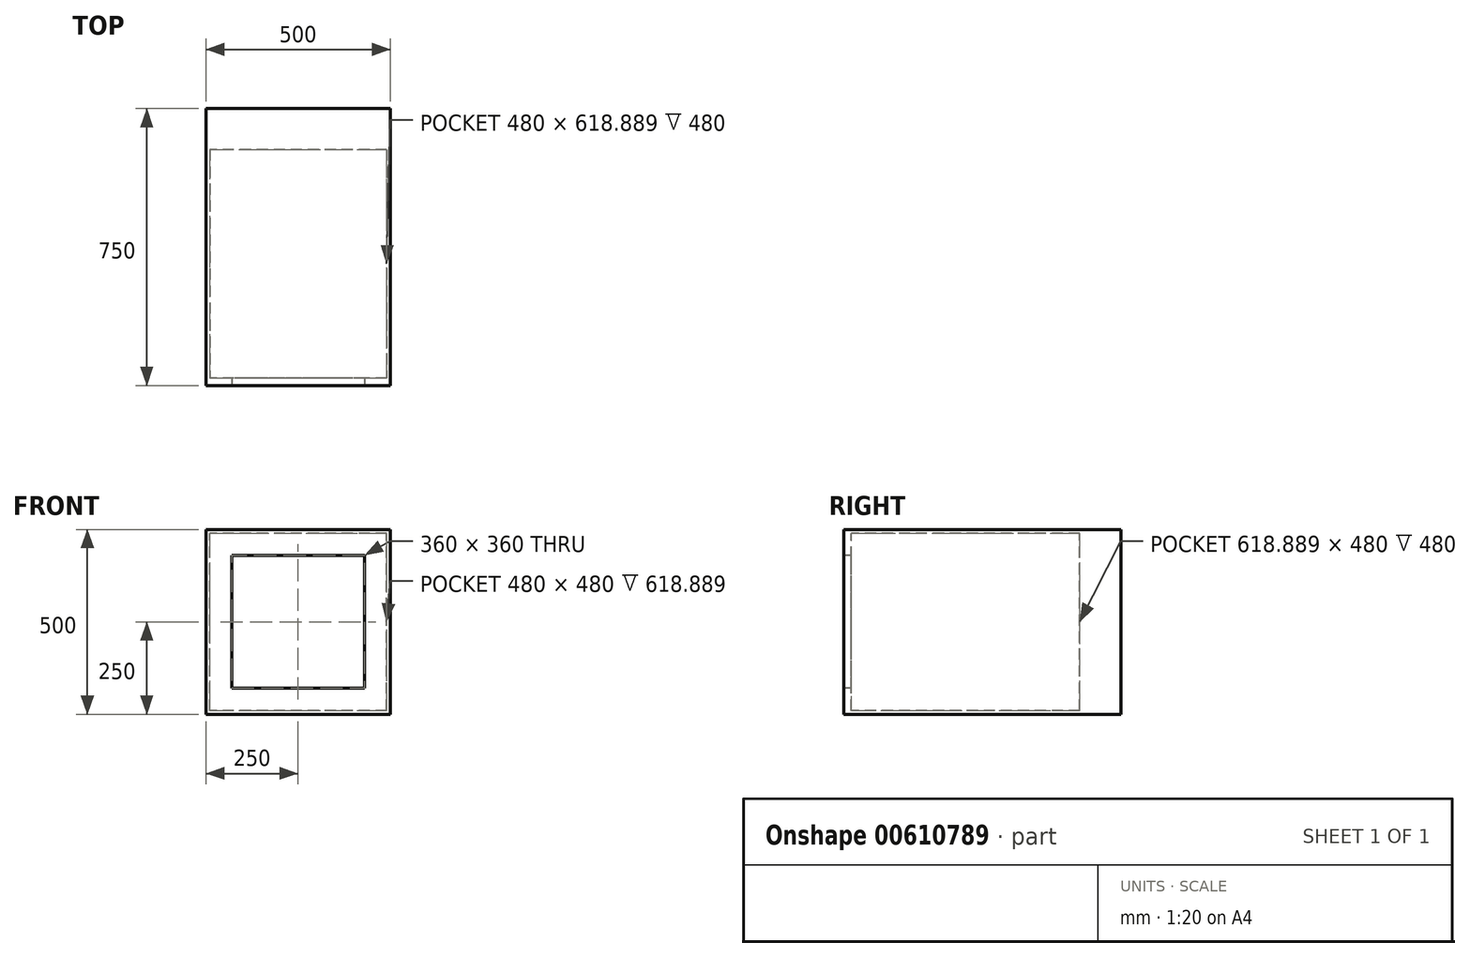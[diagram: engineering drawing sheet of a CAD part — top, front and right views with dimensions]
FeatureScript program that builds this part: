
annotation { "Feature Type Name" : "Feature", "Feature Type Description" : "" }
export const myFeature = defineFeature(function(context is Context, id is Id, definition is map)
    precondition{}
    {
        {
            var Q0;
            Q0=qCreatedBy(makeId("Front.planeOp"),FACE);
            var sketch = newSketch(context, id + "F0", { "sketchPlane" : qUnion([Q0])});
            skLineSegment(sketch, "E0.bottom", {"start": v(0, 0) * mm, "end": v(500, 0) * mm});
            skLineSegment(sketch, "E0.top", {"start": v(0, 500) * mm, "end": v(500, 500) * mm});
            skLineSegment(sketch, "E0.left", {"start": v(0, 0) * mm, "end": v(0, 500) * mm});
            skLineSegment(sketch, "E0.right", {"start": v(500, 0) * mm, "end": v(500, 500) * mm});
            skSolve(sketch);
        }
        {
            var Q0;
            Q0 = qSketchRegion(id + "F0", true);
            extrude(context, id + "F1", {"entities" : qUnion([Q0]), "depth" : 750 * mm, "offsetDistance" : 25 * mm});
        }
        {
            var Q0;
            Q0=makeQuery(id+"F1.opExtrude","CAP_FACE",FACE,{"disambiguationData":[OSD([sQuery(id+"F0.wireOp",EDGE,"E0.bottom"),sQuery(id+"F0.wireOp",EDGE,"E0.top"),sQuery(id+"F0.wireOp",EDGE,"E0.left"),sQuery(id+"F0.wireOp",EDGE,"E0.right")])],"isStart":false});
            var sketch = newSketch(context, id + "F2", { "sketchPlane" : qUnion([Q0])});
            skLineSegment(sketch, "E1", {"start": v(0, 0) * mm, "end": v(500, 500) * mm});
            skLineSegment(sketch, "E2.bottom", {"start": v(430, 70) * mm, "end": v(70, 70) * mm});
            skLineSegment(sketch, "E2.top", {"start": v(430, 430) * mm, "end": v(70, 430) * mm});
            skLineSegment(sketch, "E2.left", {"start": v(430, 70) * mm, "end": v(430, 430) * mm});
            skLineSegment(sketch, "E2.right", {"start": v(70, 70) * mm, "end": v(70, 430) * mm});
            skPoint(sketch, "E2.middle", {"position": v(250, 250) * mm});
            skSolve(sketch);
        }
        {
            var Q0;
            Q0 = qSketchRegion(id + "F2", true);
            extrude(context, id + "F3", {"entities" : qUnion([Q0]), "operationType" : NewBodyOperationType.REMOVE, "oppositeDirection" : true, "depth" : 20 * mm, "offsetDistance" : 25 * mm});
        }
        {
            var Q0;
            Q0=makeQuery(id+"F3.boolean.opBoolean","COPY",FACE,{"derivedFrom":makeQuery(id+"F3.opExtrude","CAP_FACE",FACE,{"disambiguationData":[OSD([sQuery(id+"F2.wireOp",EDGE,"E2.bottom"),sQuery(id+"F2.wireOp",EDGE,"E2.top"),sQuery(id+"F2.wireOp",EDGE,"E2.left"),sQuery(id+"F2.wireOp",EDGE,"E2.right")])],"isStart":false})});
            var sketch = newSketch(context, id + "F4", { "sketchPlane" : qUnion([Q0])});
            skLineSegment(sketch, "E3", {"start": v(70, 70) * mm, "end": v(430, 430) * mm});
            skLineSegment(sketch, "E4.bottom", {"start": v(490, 10) * mm, "end": v(10, 10) * mm});
            skLineSegment(sketch, "E4.top", {"start": v(490, 490) * mm, "end": v(10, 490) * mm});
            skLineSegment(sketch, "E4.left", {"start": v(490, 10) * mm, "end": v(490, 490) * mm});
            skLineSegment(sketch, "E4.right", {"start": v(10, 10) * mm, "end": v(10, 490) * mm});
            skPoint(sketch, "E4.middle", {"position": v(250, 250) * mm});
            skSolve(sketch);
        }
        {
            var Q0;
            Q0 = qSketchRegion(id + "F4", true);
            extrude(context, id + "F5", {"entities" : qUnion([Q0]), "operationType" : NewBodyOperationType.REMOVE, "oppositeDirection" : true, "depth" : 618.9 * mm, "offsetDistance" : 25 * mm});
        }
    });
